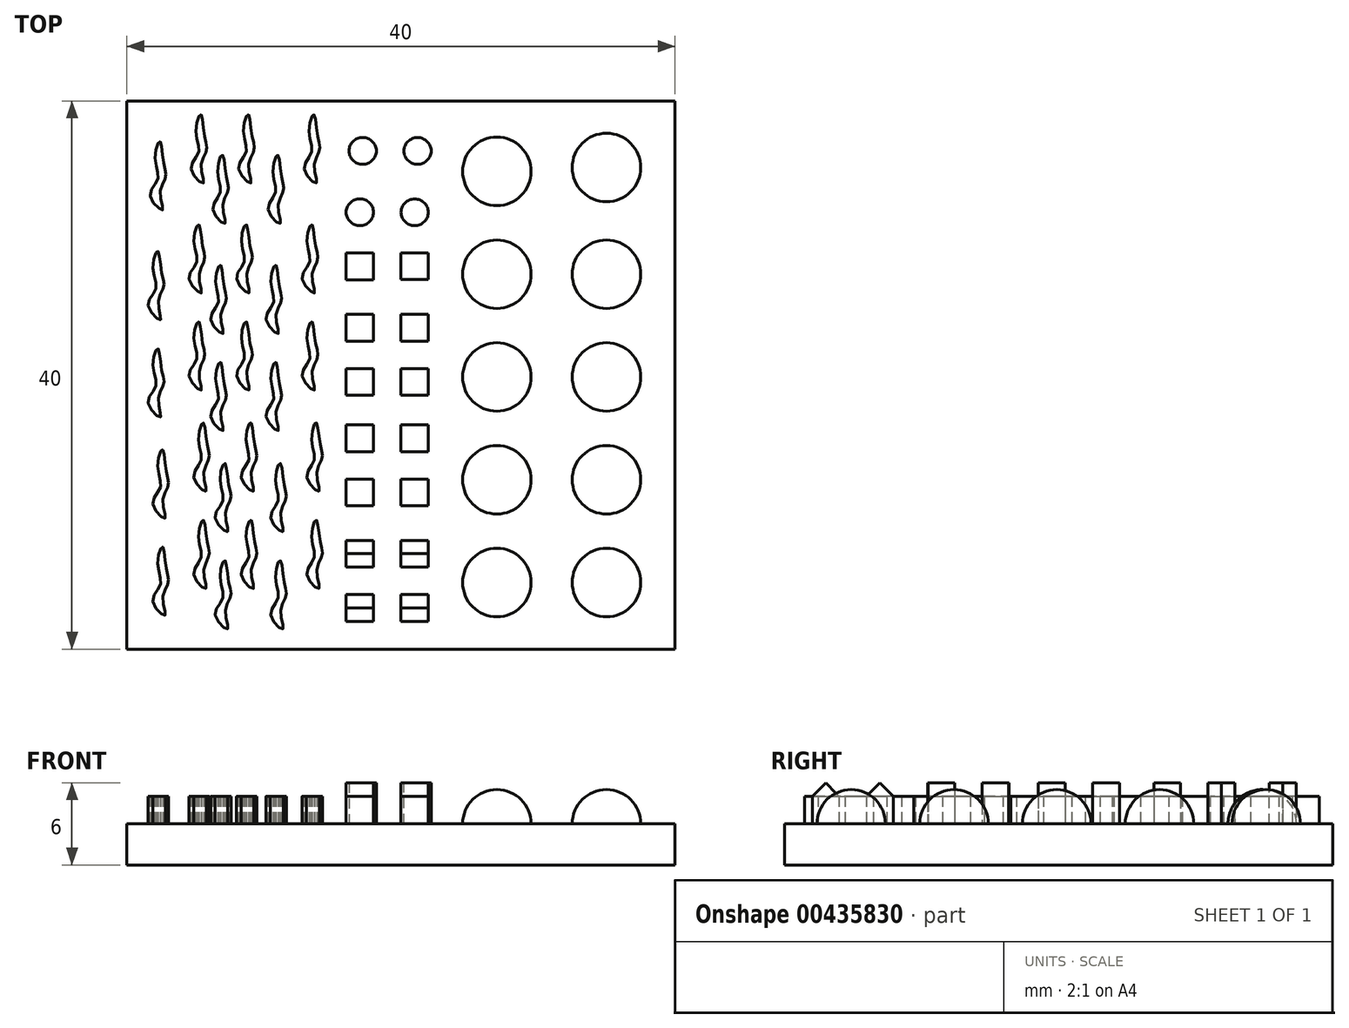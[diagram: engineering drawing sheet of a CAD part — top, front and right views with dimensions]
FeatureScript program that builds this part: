
annotation { "Feature Type Name" : "Feature", "Feature Type Description" : "" }
export const myFeature = defineFeature(function(context is Context, id is Id, definition is map)
    precondition{}
    {
        {
            var Q0;
            Q0=qCreatedBy(makeId("Top.planeOp"),FACE);
            var sketch = newSketch(context, id + "F0", { "sketchPlane" : qUnion([Q0])});
            skLineSegment(sketch, "E0.bottom", {"start": v(0, 0) * mm, "end": v(-40, 0) * mm});
            skLineSegment(sketch, "E0.top", {"start": v(0, 40) * mm, "end": v(-40, 40) * mm});
            skLineSegment(sketch, "E0.left", {"start": v(0, 0) * mm, "end": v(0, 40) * mm});
            skLineSegment(sketch, "E0.right", {"start": v(-40, 0) * mm, "end": v(-40, 40) * mm});
            skSolve(sketch);
        }
        {
            var Q0;
            Q0 = qSketchRegion(id + "F0", true);
            extrude(context, id + "F1", {"entities" : qUnion([Q0]), "depth" : 3 * mm});
        }
        {
            var Q0;
            Q0=makeQuery(id+"F1.opExtrude","CAP_FACE",FACE,{"disambiguationData":[OSD([sQuery(id+"F0.wireOp",EDGE,"E0.bottom"),sQuery(id+"F0.wireOp",EDGE,"E0.top"),sQuery(id+"F0.wireOp",EDGE,"E0.left"),sQuery(id+"F0.wireOp",EDGE,"E0.right")])],"isStart":false});
            var sketch = newSketch(context, id + "F2", { "sketchPlane" : qUnion([Q0])});
            skLineSegment(sketch, "E1", {"start": v(0, 0) * mm, "end": v(-10, 0) * mm});
            skPoint(sketch, "E2.end.orphan", {"position": v(-5, 0) * mm});
            skLineSegment(sketch, "E3", {"start": v(0, 0) * mm, "end": v(-5, 0) * mm});
            skArc(sketch, "E4", {"start": v(-5, 32.64) * mm, "mid": v(-2.5, 35.14) * mm, "end": v(-5, 37.64) * mm});
            skLineSegment(sketch, "E5", {"start": v(-5, 37.64) * mm, "end": v(-5, 40) * mm});
            skLineSegment(sketch, "E6", {"start": v(-5, 37.64) * mm, "end": v(-5, 32.64) * mm, "construction": true});
            skLineSegment(sketch, "E7", {"start": v(-5, 37.64) * mm, "end": v(-5, 32.64) * mm});
            skLineSegment(sketch, "E8", {"start": v(-5, 32.64) * mm, "end": v(-5, 30.14) * mm});
            skLineSegment(sketch, "E9", {"start": v(-5, 40) * mm, "end": v(0, 40) * mm});
            skSolve(sketch);
        }
        {
            var Q0;
            Q0=makeQuery(id+"F1.opExtrude","CAP_FACE",FACE,{"disambiguationData":[OSD([sQuery(id+"F0.wireOp",EDGE,"E0.bottom"),sQuery(id+"F0.wireOp",EDGE,"E0.top"),sQuery(id+"F0.wireOp",EDGE,"E0.left"),sQuery(id+"F0.wireOp",EDGE,"E0.right")])],"isStart":false});
            var sketch = newSketch(context, id + "F3", { "sketchPlane" : qUnion([Q0])});
            skFitSpline(sketch, "E10", {"points": [v(-37.76, 6.25) * mm, v(-37.56, 4.7) * mm, v(-38.1, 3.49) * mm, v(-37.23, 2.46) * mm, v(-37.38, 3.69) * mm, v(-36.98, 4.9) * mm, v(-37.13, 5.9) * mm, v(-37.41, 7.46) * mm, v(-37.76, 6.25) * mm]});
            skFitSpline(sketch, "E11", {"points": [v(-37.76, 13.34) * mm, v(-37.56, 11.8) * mm, v(-38.1, 10.58) * mm, v(-37.23, 9.55) * mm, v(-37.38, 10.78) * mm, v(-36.98, 11.98) * mm, v(-37.13, 13) * mm, v(-37.41, 14.56) * mm, v(-37.76, 13.34) * mm]});
            skFitSpline(sketch, "E12", {"points": [v(-38.1, 20.72) * mm, v(-37.9, 19.17) * mm, v(-38.44, 17.96) * mm, v(-37.56, 16.93) * mm, v(-37.72, 18.16) * mm, v(-37.31, 19.36) * mm, v(-37.46, 20.38) * mm, v(-37.75, 21.94) * mm, v(-38.1, 20.72) * mm]});
            skFitSpline(sketch, "E13", {"points": [v(-38.1, 27.81) * mm, v(-37.9, 26.26) * mm, v(-38.44, 25.05) * mm, v(-37.56, 24.02) * mm, v(-37.72, 25.25) * mm, v(-37.31, 26.45) * mm, v(-37.46, 27.47) * mm, v(-37.75, 29.03) * mm, v(-38.1, 27.81) * mm]});
            skFitSpline(sketch, "E14", {"points": [v(-37.94, 35.84) * mm, v(-37.75, 34.29) * mm, v(-38.3, 33.07) * mm, v(-37.41, 32.05) * mm, v(-37.57, 33.27) * mm, v(-37.16, 34.48) * mm, v(-37.32, 35.5) * mm, v(-37.6, 37.05) * mm, v(-37.94, 35.84) * mm]});
            skFitSpline(sketch, "E15", {"points": [v(-34.78, 8.21) * mm, v(-34.58, 6.66) * mm, v(-35.13, 5.45) * mm, v(-34.25, 4.42) * mm, v(-34.4, 5.65) * mm, v(-34, 6.85) * mm, v(-34.15, 7.87) * mm, v(-34.44, 9.42) * mm, v(-34.78, 8.21) * mm]});
            skFitSpline(sketch, "E16", {"points": [v(-34.78, 15.3) * mm, v(-34.58, 13.75) * mm, v(-35.13, 12.54) * mm, v(-34.25, 11.5) * mm, v(-34.4, 12.74) * mm, v(-34, 13.94) * mm, v(-34.15, 14.96) * mm, v(-34.44, 16.52) * mm, v(-34.78, 15.3) * mm]});
            skFitSpline(sketch, "E17", {"points": [v(-35.11, 22.68) * mm, v(-34.92, 21.13) * mm, v(-35.46, 19.92) * mm, v(-34.58, 18.9) * mm, v(-34.74, 20.12) * mm, v(-34.33, 21.32) * mm, v(-34.48, 22.34) * mm, v(-34.77, 23.9) * mm, v(-35.11, 22.68) * mm]});
            skFitSpline(sketch, "E18", {"points": [v(-35.11, 29.77) * mm, v(-34.92, 28.22) * mm, v(-35.46, 27.01) * mm, v(-34.58, 25.98) * mm, v(-34.74, 27.2) * mm, v(-34.33, 28.41) * mm, v(-34.48, 29.43) * mm, v(-34.77, 30.99) * mm, v(-35.11, 29.77) * mm]});
            skFitSpline(sketch, "E19", {"points": [v(-34.97, 37.8) * mm, v(-34.77, 36.25) * mm, v(-35.31, 35.03) * mm, v(-34.44, 34) * mm, v(-34.59, 35.23) * mm, v(-34.18, 36.44) * mm, v(-34.34, 37.45) * mm, v(-34.62, 39.01) * mm, v(-34.97, 37.8) * mm]});
            skFitSpline(sketch, "E20", {"points": [v(-33.2, 5.26) * mm, v(-33, 3.7) * mm, v(-33.55, 2.5) * mm, v(-32.67, 1.46) * mm, v(-32.82, 2.69) * mm, v(-32.42, 3.9) * mm, v(-32.57, 4.91) * mm, v(-32.86, 6.47) * mm, v(-33.2, 5.26) * mm]});
            skFitSpline(sketch, "E21", {"points": [v(-33.2, 12.35) * mm, v(-33, 10.8) * mm, v(-33.55, 9.58) * mm, v(-32.67, 8.55) * mm, v(-32.82, 9.78) * mm, v(-32.42, 10.99) * mm, v(-32.57, 12) * mm, v(-32.86, 13.56) * mm, v(-33.2, 12.35) * mm]});
            skFitSpline(sketch, "E22", {"points": [v(-33.53, 19.73) * mm, v(-33.34, 18.18) * mm, v(-33.88, 16.97) * mm, v(-33, 15.94) * mm, v(-33.16, 17.16) * mm, v(-32.75, 18.37) * mm, v(-32.9, 19.38) * mm, v(-33.19, 20.94) * mm, v(-33.53, 19.73) * mm]});
            skFitSpline(sketch, "E23", {"points": [v(-33.53, 26.82) * mm, v(-33.34, 25.27) * mm, v(-33.88, 24.06) * mm, v(-33, 23.03) * mm, v(-33.16, 24.25) * mm, v(-32.75, 25.46) * mm, v(-32.9, 26.47) * mm, v(-33.19, 28.03) * mm, v(-33.53, 26.82) * mm]});
            skFitSpline(sketch, "E24", {"points": [v(-33.39, 34.84) * mm, v(-33.19, 33.3) * mm, v(-33.73, 32.08) * mm, v(-32.86, 31.05) * mm, v(-33, 32.28) * mm, v(-32.6, 33.48) * mm, v(-32.76, 34.5) * mm, v(-33.04, 36.06) * mm, v(-33.39, 34.84) * mm]});
            skFitSpline(sketch, "E25", {"points": [v(-31.3, 8.21) * mm, v(-31.11, 6.66) * mm, v(-31.66, 5.45) * mm, v(-30.78, 4.42) * mm, v(-30.93, 5.65) * mm, v(-30.53, 6.85) * mm, v(-30.68, 7.87) * mm, v(-30.97, 9.42) * mm, v(-31.3, 8.21) * mm]});
            skFitSpline(sketch, "E26", {"points": [v(-31.3, 15.3) * mm, v(-31.11, 13.75) * mm, v(-31.66, 12.54) * mm, v(-30.78, 11.5) * mm, v(-30.93, 12.74) * mm, v(-30.53, 13.94) * mm, v(-30.68, 14.96) * mm, v(-30.97, 16.52) * mm, v(-31.3, 15.3) * mm]});
            skFitSpline(sketch, "E27", {"points": [v(-31.64, 22.68) * mm, v(-31.45, 21.13) * mm, v(-32, 19.92) * mm, v(-31.11, 18.9) * mm, v(-31.27, 20.12) * mm, v(-30.86, 21.32) * mm, v(-31.02, 22.34) * mm, v(-31.3, 23.9) * mm, v(-31.64, 22.68) * mm]});
            skFitSpline(sketch, "E28", {"points": [v(-31.64, 29.77) * mm, v(-31.45, 28.22) * mm, v(-32, 27.01) * mm, v(-31.11, 25.98) * mm, v(-31.27, 27.2) * mm, v(-30.86, 28.41) * mm, v(-31.02, 29.43) * mm, v(-31.3, 30.99) * mm, v(-31.64, 29.77) * mm]});
            skFitSpline(sketch, "E29", {"points": [v(-31.5, 37.8) * mm, v(-31.3, 36.25) * mm, v(-31.85, 35.03) * mm, v(-30.97, 34) * mm, v(-31.12, 35.23) * mm, v(-30.71, 36.44) * mm, v(-30.87, 37.45) * mm, v(-31.15, 39.01) * mm, v(-31.5, 37.8) * mm]});
            skFitSpline(sketch, "E30", {"points": [v(-29.16, 5.26) * mm, v(-28.97, 3.7) * mm, v(-29.51, 2.5) * mm, v(-28.63, 1.46) * mm, v(-28.79, 2.69) * mm, v(-28.38, 3.9) * mm, v(-28.54, 4.91) * mm, v(-28.82, 6.47) * mm, v(-29.16, 5.26) * mm]});
            skFitSpline(sketch, "E31", {"points": [v(-29.16, 12.35) * mm, v(-28.97, 10.8) * mm, v(-29.51, 9.58) * mm, v(-28.63, 8.55) * mm, v(-28.79, 9.78) * mm, v(-28.38, 10.99) * mm, v(-28.54, 12) * mm, v(-28.82, 13.56) * mm, v(-29.16, 12.35) * mm]});
            skFitSpline(sketch, "E32", {"points": [v(-29.5, 19.73) * mm, v(-29.3, 18.18) * mm, v(-29.85, 16.97) * mm, v(-28.97, 15.94) * mm, v(-29.12, 17.16) * mm, v(-28.72, 18.37) * mm, v(-28.87, 19.38) * mm, v(-29.15, 20.94) * mm, v(-29.5, 19.73) * mm]});
            skFitSpline(sketch, "E33", {"points": [v(-29.5, 26.82) * mm, v(-29.3, 25.27) * mm, v(-29.85, 24.06) * mm, v(-28.97, 23.03) * mm, v(-29.12, 24.25) * mm, v(-28.72, 25.46) * mm, v(-28.87, 26.47) * mm, v(-29.15, 28.03) * mm, v(-29.5, 26.82) * mm]});
            skFitSpline(sketch, "E34", {"points": [v(-29.35, 34.84) * mm, v(-29.15, 33.3) * mm, v(-29.7, 32.08) * mm, v(-28.82, 31.05) * mm, v(-28.97, 32.28) * mm, v(-28.57, 33.48) * mm, v(-28.72, 34.5) * mm, v(-29, 36.06) * mm, v(-29.35, 34.84) * mm]});
            skFitSpline(sketch, "E35", {"points": [v(-26.53, 8.21) * mm, v(-26.33, 6.66) * mm, v(-26.88, 5.45) * mm, v(-26, 4.42) * mm, v(-26.15, 5.65) * mm, v(-25.75, 6.85) * mm, v(-25.9, 7.87) * mm, v(-26.18, 9.42) * mm, v(-26.53, 8.21) * mm]});
            skFitSpline(sketch, "E36", {"points": [v(-26.53, 15.3) * mm, v(-26.33, 13.75) * mm, v(-26.88, 12.54) * mm, v(-26, 11.5) * mm, v(-26.15, 12.74) * mm, v(-25.75, 13.94) * mm, v(-25.9, 14.96) * mm, v(-26.18, 16.52) * mm, v(-26.53, 15.3) * mm]});
            skFitSpline(sketch, "E37", {"points": [v(-26.86, 22.68) * mm, v(-26.67, 21.13) * mm, v(-27.21, 19.92) * mm, v(-26.33, 18.9) * mm, v(-26.49, 20.12) * mm, v(-26.08, 21.32) * mm, v(-26.23, 22.34) * mm, v(-26.52, 23.9) * mm, v(-26.86, 22.68) * mm]});
            skFitSpline(sketch, "E38", {"points": [v(-26.86, 29.77) * mm, v(-26.67, 28.22) * mm, v(-27.21, 27.01) * mm, v(-26.33, 25.98) * mm, v(-26.49, 27.2) * mm, v(-26.08, 28.41) * mm, v(-26.23, 29.43) * mm, v(-26.52, 30.99) * mm, v(-26.86, 29.77) * mm]});
            skFitSpline(sketch, "E39", {"points": [v(-26.71, 37.8) * mm, v(-26.52, 36.25) * mm, v(-27.06, 35.03) * mm, v(-26.18, 34) * mm, v(-26.34, 35.23) * mm, v(-25.93, 36.44) * mm, v(-26.09, 37.45) * mm, v(-26.37, 39.01) * mm, v(-26.71, 37.8) * mm]});
            skSolve(sketch);
        }
        {
            var Q0;
            Q0 = qSketchRegion(id + "F3", true);
            extrude(context, id + "F4", {"entities" : qUnion([Q0]), "operationType" : NewBodyOperationType.ADD, "depth" : 2 * mm});
        }
        {
            var Q0;
            Q0=makeQuery(id+"F2.imprint","IMPRINT",FACE,{"disambiguationData":[TD([[makeQuery(id+"F2.imprint","IMPRINT",EDGE,{"derivedFrom":sQuery(id+"F2.wireOp",EDGE,"E4")}),1.0]])]});
            var Q1;
            Q1=sQuery(id+"F2.wireOp",EDGE,"E7");
            revolve(context, id + "F5", {"operationType" : NewBodyOperationType.ADD, "entities" : qUnion([Q0]), "axis" : qUnion([Q1]), "revolveType" : RevolveType.FULL});
        }
        {
            var Q0;
            Q0=makeQuery(id+"F1.opExtrude","CAP_FACE",FACE,{"disambiguationData":[OSD([sQuery(id+"F0.wireOp",EDGE,"E0.bottom"),sQuery(id+"F0.wireOp",EDGE,"E0.top"),sQuery(id+"F0.wireOp",EDGE,"E0.left"),sQuery(id+"F0.wireOp",EDGE,"E0.right")])],"isStart":false});
            var sketch = newSketch(context, id + "F6", { "sketchPlane" : qUnion([Q0])});
            skLineSegment(sketch, "E40", {"start": v(0, 0) * mm, "end": v(-5, 0) * mm});
            skLineSegment(sketch, "E41", {"start": v(-5, 0) * mm, "end": v(-5, 2.36) * mm});
            skArc(sketch, "E42", {"start": v(-5, 2.36) * mm, "mid": v(-2.5, 4.86) * mm, "end": v(-5, 7.36) * mm});
            skLineSegment(sketch, "E43", {"start": v(-5, 2.36) * mm, "end": v(-5, 7.36) * mm});
            skLineSegment(sketch, "E44", {"start": v(-5, 7.36) * mm, "end": v(-5, 2.36) * mm, "construction": true});
            skSolve(sketch);
        }
        {
            var Q0;
            Q0 = qSketchRegion(id + "F6", true);
            var Q1;
            Q1=sQuery(id+"F6.wireOp",EDGE,"E43");
            revolve(context, id + "F7", {"operationType" : NewBodyOperationType.ADD, "entities" : qUnion([Q0]), "axis" : qUnion([Q1]), "revolveType" : RevolveType.FULL});
        }
        {
            var Q0;
            Q0=makeQuery(id+"F1.opExtrude","CAP_FACE",FACE,{"disambiguationData":[OSD([sQuery(id+"F0.wireOp",EDGE,"E0.bottom"),sQuery(id+"F0.wireOp",EDGE,"E0.top"),sQuery(id+"F0.wireOp",EDGE,"E0.left"),sQuery(id+"F0.wireOp",EDGE,"E0.right")])],"isStart":false});
            var sketch = newSketch(context, id + "F8", { "sketchPlane" : qUnion([Q0])});
            skLineSegment(sketch, "E45", {"start": v(0, 0) * mm, "end": v(-5, 0) * mm});
            skLineSegment(sketch, "E46", {"start": v(-5, 0) * mm, "end": v(-5, 7.36) * mm});
            skLineSegment(sketch, "E47", {"start": v(-5, 7.36) * mm, "end": v(-5, 9.86) * mm});
            skArc(sketch, "E48", {"start": v(-5, 9.86) * mm, "mid": v(-2.5, 12.36) * mm, "end": v(-5, 14.86) * mm});
            skLineSegment(sketch, "E49", {"start": v(-5, 9.86) * mm, "end": v(-5, 14.86) * mm});
            skLineSegment(sketch, "E50", {"start": v(-5, 14.86) * mm, "end": v(-5, 9.86) * mm, "construction": true});
            skSolve(sketch);
        }
        {
            var Q0;
            Q0 = qSketchRegion(id + "F8", true);
            var Q1;
            Q1=sQuery(id+"F8.wireOp",EDGE,"E49");
            revolve(context, id + "F9", {"operationType" : NewBodyOperationType.ADD, "entities" : qUnion([Q0]), "axis" : qUnion([Q1]), "revolveType" : RevolveType.FULL});
        }
        {
            var Q0;
            Q0=makeQuery(id+"F1.opExtrude","CAP_FACE",FACE,{"disambiguationData":[OSD([sQuery(id+"F0.wireOp",EDGE,"E0.bottom"),sQuery(id+"F0.wireOp",EDGE,"E0.top"),sQuery(id+"F0.wireOp",EDGE,"E0.left"),sQuery(id+"F0.wireOp",EDGE,"E0.right")])],"isStart":false});
            var sketch = newSketch(context, id + "F10", { "sketchPlane" : qUnion([Q0])});
            skLineSegment(sketch, "E51", {"start": v(0, 0) * mm, "end": v(-5, 0) * mm});
            skLineSegment(sketch, "E52", {"start": v(-5, 0) * mm, "end": v(-5, 14.86) * mm});
            skLineSegment(sketch, "E53", {"start": v(-5, 14.86) * mm, "end": v(-5, 17.36) * mm});
            skArc(sketch, "E54", {"start": v(-5, 17.36) * mm, "mid": v(-2.5, 19.86) * mm, "end": v(-5, 22.36) * mm});
            skLineSegment(sketch, "E55", {"start": v(-5, 17.36) * mm, "end": v(-5, 22.36) * mm});
            skLineSegment(sketch, "E56", {"start": v(-5, 22.36) * mm, "end": v(-5, 17.36) * mm, "construction": true});
            skSolve(sketch);
        }
        {
            var Q0;
            Q0 = qSketchRegion(id + "F10", true);
            var Q1;
            Q1=sQuery(id+"F10.wireOp",EDGE,"E55");
            revolve(context, id + "F11", {"operationType" : NewBodyOperationType.ADD, "entities" : qUnion([Q0]), "axis" : qUnion([Q1]), "revolveType" : RevolveType.FULL});
        }
        {
            var Q0;
            Q0=makeQuery(id+"F1.opExtrude","CAP_FACE",FACE,{"disambiguationData":[OSD([sQuery(id+"F0.wireOp",EDGE,"E0.bottom"),sQuery(id+"F0.wireOp",EDGE,"E0.top"),sQuery(id+"F0.wireOp",EDGE,"E0.left"),sQuery(id+"F0.wireOp",EDGE,"E0.right")])],"isStart":false});
            var sketch = newSketch(context, id + "F12", { "sketchPlane" : qUnion([Q0])});
            skLineSegment(sketch, "E57", {"start": v(0, 0) * mm, "end": v(-5, 0) * mm});
            skLineSegment(sketch, "E58", {"start": v(-5, 0) * mm, "end": v(-5, 22.36) * mm});
            skLineSegment(sketch, "E59", {"start": v(-5, 22.36) * mm, "end": v(-5, 24.86) * mm});
            skArc(sketch, "E60", {"start": v(-5, 24.86) * mm, "mid": v(-2.5, 27.36) * mm, "end": v(-5, 29.86) * mm});
            skLineSegment(sketch, "E61", {"start": v(-5, 24.86) * mm, "end": v(-5, 29.86) * mm});
            skLineSegment(sketch, "E62", {"start": v(-5, 29.86) * mm, "end": v(-5, 24.86) * mm, "construction": true});
            skSolve(sketch);
        }
        {
            var Q0;
            Q0 = qSketchRegion(id + "F12", true);
            var Q1;
            Q1=sQuery(id+"F12.wireOp",EDGE,"E61");
            revolve(context, id + "F13", {"operationType" : NewBodyOperationType.ADD, "entities" : qUnion([Q0]), "axis" : qUnion([Q1]), "revolveType" : RevolveType.FULL});
        }
        {
            var Q0;
            Q0=makeQuery(id+"F1.opExtrude","CAP_FACE",FACE,{"disambiguationData":[OSD([sQuery(id+"F0.wireOp",EDGE,"E0.bottom"),sQuery(id+"F0.wireOp",EDGE,"E0.top"),sQuery(id+"F0.wireOp",EDGE,"E0.left"),sQuery(id+"F0.wireOp",EDGE,"E0.right")])],"isStart":false});
            var sketch = newSketch(context, id + "F14", { "sketchPlane" : qUnion([Q0])});
            skLineSegment(sketch, "E63", {"start": v(0, 0) * mm, "end": v(-13, 0) * mm});
            skLineSegment(sketch, "E64", {"start": v(-13, 0) * mm, "end": v(-13, 2.36) * mm});
            skArc(sketch, "E65", {"start": v(-13, 2.36) * mm, "mid": v(-10.5, 4.86) * mm, "end": v(-13, 7.36) * mm});
            skLineSegment(sketch, "E66", {"start": v(-13, 2.36) * mm, "end": v(-13, 7.36) * mm});
            skLineSegment(sketch, "E67", {"start": v(-13, 7.36) * mm, "end": v(-13, 2.36) * mm, "construction": true});
            skSolve(sketch);
        }
        {
            var Q0;
            Q0 = qSketchRegion(id + "F14", true);
            var Q1;
            Q1=sQuery(id+"F14.wireOp",EDGE,"E66");
            revolve(context, id + "F15", {"operationType" : NewBodyOperationType.ADD, "entities" : qUnion([Q0]), "axis" : qUnion([Q1]), "revolveType" : RevolveType.FULL});
        }
        {
            var Q0;
            Q0=makeQuery(id+"F1.opExtrude","CAP_FACE",FACE,{"disambiguationData":[OSD([sQuery(id+"F0.wireOp",EDGE,"E0.bottom"),sQuery(id+"F0.wireOp",EDGE,"E0.top"),sQuery(id+"F0.wireOp",EDGE,"E0.left"),sQuery(id+"F0.wireOp",EDGE,"E0.right")])],"isStart":false});
            var sketch = newSketch(context, id + "F16", { "sketchPlane" : qUnion([Q0])});
            skLineSegment(sketch, "E68", {"start": v(0, 0) * mm, "end": v(-13, 0) * mm});
            skLineSegment(sketch, "E69", {"start": v(-13, 0) * mm, "end": v(-13, 7.36) * mm});
            skLineSegment(sketch, "E70", {"start": v(-13, 7.36) * mm, "end": v(-13, 9.86) * mm});
            skArc(sketch, "E71", {"start": v(-13, 9.86) * mm, "mid": v(-10.5, 12.36) * mm, "end": v(-13, 14.86) * mm});
            skLineSegment(sketch, "E72", {"start": v(-13, 9.86) * mm, "end": v(-13, 14.86) * mm});
            skLineSegment(sketch, "E73", {"start": v(-13, 14.86) * mm, "end": v(-13, 9.86) * mm, "construction": true});
            skSolve(sketch);
        }
        {
            var Q0;
            Q0 = qSketchRegion(id + "F16", true);
            var Q1;
            Q1=sQuery(id+"F16.wireOp",EDGE,"E72");
            revolve(context, id + "F17", {"operationType" : NewBodyOperationType.ADD, "entities" : qUnion([Q0]), "axis" : qUnion([Q1]), "revolveType" : RevolveType.FULL});
        }
        {
            var Q0;
            Q0=makeQuery(id+"F1.opExtrude","CAP_FACE",FACE,{"disambiguationData":[OSD([sQuery(id+"F0.wireOp",EDGE,"E0.bottom"),sQuery(id+"F0.wireOp",EDGE,"E0.top"),sQuery(id+"F0.wireOp",EDGE,"E0.left"),sQuery(id+"F0.wireOp",EDGE,"E0.right")])],"isStart":false});
            var sketch = newSketch(context, id + "F18", { "sketchPlane" : qUnion([Q0])});
            skLineSegment(sketch, "E74", {"start": v(0, 0) * mm, "end": v(-13, 0) * mm});
            skLineSegment(sketch, "E75", {"start": v(-13, 0) * mm, "end": v(-13, 14.86) * mm});
            skLineSegment(sketch, "E76", {"start": v(-13, 14.86) * mm, "end": v(-13, 17.36) * mm});
            skArc(sketch, "E77", {"start": v(-13, 17.36) * mm, "mid": v(-10.5, 19.86) * mm, "end": v(-13, 22.36) * mm});
            skLineSegment(sketch, "E78", {"start": v(-13, 17.36) * mm, "end": v(-13, 22.36) * mm});
            skLineSegment(sketch, "E79", {"start": v(-13, 22.36) * mm, "end": v(-13, 17.36) * mm, "construction": true});
            skSolve(sketch);
        }
        {
            var Q0;
            Q0 = qSketchRegion(id + "F18", true);
            var Q1;
            Q1=sQuery(id+"F18.wireOp",EDGE,"E78");
            revolve(context, id + "F19", {"operationType" : NewBodyOperationType.ADD, "entities" : qUnion([Q0]), "axis" : qUnion([Q1]), "revolveType" : RevolveType.FULL});
        }
        {
            var Q0;
            Q0=makeQuery(id+"F1.opExtrude","CAP_FACE",FACE,{"disambiguationData":[OSD([sQuery(id+"F0.wireOp",EDGE,"E0.bottom"),sQuery(id+"F0.wireOp",EDGE,"E0.top"),sQuery(id+"F0.wireOp",EDGE,"E0.left"),sQuery(id+"F0.wireOp",EDGE,"E0.right")])],"isStart":false});
            var sketch = newSketch(context, id + "F20", { "sketchPlane" : qUnion([Q0])});
            skLineSegment(sketch, "E80", {"start": v(0, 0) * mm, "end": v(-13, 0) * mm});
            skLineSegment(sketch, "E81", {"start": v(-13, 0) * mm, "end": v(-13, 22.36) * mm});
            skLineSegment(sketch, "E82", {"start": v(-13, 22.36) * mm, "end": v(-13, 24.86) * mm});
            skArc(sketch, "E83", {"start": v(-13, 24.86) * mm, "mid": v(-10.5, 27.36) * mm, "end": v(-13, 29.86) * mm});
            skLineSegment(sketch, "E84", {"start": v(-13, 24.86) * mm, "end": v(-13, 29.86) * mm});
            skLineSegment(sketch, "E85", {"start": v(-13, 29.86) * mm, "end": v(-13, 24.86) * mm, "construction": true});
            skSolve(sketch);
        }
        {
            var Q0;
            Q0 = qSketchRegion(id + "F20", true);
            var Q1;
            Q1=sQuery(id+"F20.wireOp",EDGE,"E84");
            revolve(context, id + "F21", {"operationType" : NewBodyOperationType.ADD, "entities" : qUnion([Q0]), "axis" : qUnion([Q1]), "revolveType" : RevolveType.FULL});
        }
        {
            var Q0;
            Q0=makeQuery(id+"F1.opExtrude","CAP_FACE",FACE,{"disambiguationData":[OSD([sQuery(id+"F0.wireOp",EDGE,"E0.bottom"),sQuery(id+"F0.wireOp",EDGE,"E0.top"),sQuery(id+"F0.wireOp",EDGE,"E0.left"),sQuery(id+"F0.wireOp",EDGE,"E0.right")])],"isStart":false});
            var sketch = newSketch(context, id + "F22", { "sketchPlane" : qUnion([Q0])});
            skLineSegment(sketch, "E86", {"start": v(0, 0) * mm, "end": v(-13, 0) * mm});
            skLineSegment(sketch, "E87", {"start": v(-13, 0) * mm, "end": v(-13, 29.86) * mm});
            skArc(sketch, "E88", {"start": v(-13, 32.36) * mm, "mid": v(-10.5, 34.86) * mm, "end": v(-13, 37.36) * mm});
            skLineSegment(sketch, "E89", {"start": v(-13, 32.36) * mm, "end": v(-13, 37.36) * mm});
            skLineSegment(sketch, "E90", {"start": v(-13, 37.36) * mm, "end": v(-13, 32.36) * mm, "construction": true});
            skSolve(sketch);
        }
        {
            var Q0;
            Q0 = qSketchRegion(id + "F22", true);
            var Q1;
            Q1=sQuery(id+"F22.wireOp",EDGE,"E89");
            revolve(context, id + "F23", {"operationType" : NewBodyOperationType.ADD, "entities" : qUnion([Q0]), "axis" : qUnion([Q1]), "revolveType" : RevolveType.FULL});
        }
        {
            var Q0;
            Q0=makeQuery(id+"F1.opExtrude","CAP_FACE",FACE,{"disambiguationData":[OSD([sQuery(id+"F0.wireOp",EDGE,"E0.bottom"),sQuery(id+"F0.wireOp",EDGE,"E0.top"),sQuery(id+"F0.wireOp",EDGE,"E0.left"),sQuery(id+"F0.wireOp",EDGE,"E0.right")])],"isStart":false});
            var sketch = newSketch(context, id + "F24", { "sketchPlane" : qUnion([Q0])});
            skLineSegment(sketch, "E91", {"start": v(0, 0) * mm, "end": v(-21, 0) * mm});
            skLineSegment(sketch, "E92", {"start": v(-21, 0) * mm, "end": v(-21, 3) * mm});
            skLineSegment(sketch, "E93.bottom", {"start": v(-22, 2.02) * mm, "end": v(-24, 2.02) * mm});
            skLineSegment(sketch, "E93.top", {"start": v(-22, 3.98) * mm, "end": v(-24, 3.98) * mm});
            skLineSegment(sketch, "E93.left", {"start": v(-22, 2.02) * mm, "end": v(-22, 3.98) * mm});
            skLineSegment(sketch, "E93.right", {"start": v(-24, 2.02) * mm, "end": v(-24, 3.98) * mm});
            skPoint(sketch, "E93.middle", {"position": v(-23, 3) * mm});
            skLineSegment(sketch, "E94.bottom", {"start": v(-18, 2.02) * mm, "end": v(-20, 2.02) * mm});
            skLineSegment(sketch, "E94.top", {"start": v(-18, 3.98) * mm, "end": v(-20, 3.98) * mm});
            skLineSegment(sketch, "E94.left", {"start": v(-18, 2.02) * mm, "end": v(-18, 3.98) * mm});
            skLineSegment(sketch, "E94.right", {"start": v(-20, 2.02) * mm, "end": v(-20, 3.98) * mm});
            skPoint(sketch, "E94.middle", {"position": v(-19, 3) * mm});
            skLineSegment(sketch, "E95.bottom", {"start": v(-22, 5.98) * mm, "end": v(-24, 5.98) * mm});
            skLineSegment(sketch, "E95.top", {"start": v(-22, 7.94) * mm, "end": v(-24, 7.94) * mm});
            skLineSegment(sketch, "E95.left", {"start": v(-22, 5.98) * mm, "end": v(-22, 7.94) * mm});
            skLineSegment(sketch, "E95.right", {"start": v(-24, 5.98) * mm, "end": v(-24, 7.94) * mm});
            skLineSegment(sketch, "E96.bottom", {"start": v(-18, 5.98) * mm, "end": v(-20, 5.98) * mm});
            skLineSegment(sketch, "E96.top", {"start": v(-18, 7.94) * mm, "end": v(-20, 7.94) * mm});
            skLineSegment(sketch, "E96.left", {"start": v(-18, 5.98) * mm, "end": v(-18, 7.94) * mm});
            skLineSegment(sketch, "E96.right", {"start": v(-20, 5.98) * mm, "end": v(-20, 7.94) * mm});
            skLineSegment(sketch, "E97.bottom", {"start": v(-22, 10.45) * mm, "end": v(-24, 10.45) * mm});
            skLineSegment(sketch, "E97.top", {"start": v(-22, 12.4) * mm, "end": v(-24, 12.4) * mm});
            skLineSegment(sketch, "E97.left", {"start": v(-22, 10.45) * mm, "end": v(-22, 12.4) * mm});
            skLineSegment(sketch, "E97.right", {"start": v(-24, 10.45) * mm, "end": v(-24, 12.4) * mm});
            skPoint(sketch, "E97.middle", {"position": v(-23, 11.43) * mm});
            skLineSegment(sketch, "E98.bottom", {"start": v(-18, 10.46) * mm, "end": v(-20, 10.46) * mm});
            skLineSegment(sketch, "E98.top", {"start": v(-18, 12.4) * mm, "end": v(-20, 12.4) * mm});
            skLineSegment(sketch, "E98.left", {"start": v(-18, 10.46) * mm, "end": v(-18, 12.4) * mm});
            skLineSegment(sketch, "E98.right", {"start": v(-20, 10.46) * mm, "end": v(-20, 12.4) * mm});
            skPoint(sketch, "E98.middle", {"position": v(-19, 11.43) * mm});
            skLineSegment(sketch, "E99.bottom", {"start": v(-22, 14.4) * mm, "end": v(-24, 14.4) * mm});
            skLineSegment(sketch, "E99.top", {"start": v(-22, 16.37) * mm, "end": v(-24, 16.37) * mm});
            skLineSegment(sketch, "E99.left", {"start": v(-22, 14.4) * mm, "end": v(-22, 16.37) * mm});
            skLineSegment(sketch, "E99.right", {"start": v(-24, 14.4) * mm, "end": v(-24, 16.37) * mm});
            skLineSegment(sketch, "E100.bottom", {"start": v(-18, 14.4) * mm, "end": v(-20, 14.4) * mm});
            skLineSegment(sketch, "E100.top", {"start": v(-18, 16.35) * mm, "end": v(-20, 16.35) * mm});
            skLineSegment(sketch, "E100.left", {"start": v(-18, 14.4) * mm, "end": v(-18, 16.35) * mm});
            skLineSegment(sketch, "E100.right", {"start": v(-20, 14.4) * mm, "end": v(-20, 16.35) * mm});
            skLineSegment(sketch, "E101.bottom", {"start": v(-22, 18.52) * mm, "end": v(-24, 18.52) * mm});
            skLineSegment(sketch, "E101.top", {"start": v(-22, 20.47) * mm, "end": v(-24, 20.47) * mm});
            skLineSegment(sketch, "E101.left", {"start": v(-22, 18.52) * mm, "end": v(-22, 20.47) * mm});
            skLineSegment(sketch, "E101.right", {"start": v(-24, 18.52) * mm, "end": v(-24, 20.47) * mm});
            skPoint(sketch, "E101.middle", {"position": v(-23, 19.5) * mm});
            skLineSegment(sketch, "E102.bottom", {"start": v(-18, 18.52) * mm, "end": v(-20, 18.52) * mm});
            skLineSegment(sketch, "E102.top", {"start": v(-18, 20.47) * mm, "end": v(-20, 20.47) * mm});
            skLineSegment(sketch, "E102.left", {"start": v(-18, 18.52) * mm, "end": v(-18, 20.47) * mm});
            skLineSegment(sketch, "E102.right", {"start": v(-20, 18.52) * mm, "end": v(-20, 20.47) * mm});
            skPoint(sketch, "E102.middle", {"position": v(-19, 19.5) * mm});
            skLineSegment(sketch, "E103", {"start": v(-21, 23.57) * mm, "end": v(-19, 23.57) * mm});
            skLineSegment(sketch, "E104.bottom", {"start": v(-22, 22.47) * mm, "end": v(-24, 22.47) * mm});
            skLineSegment(sketch, "E104.top", {"start": v(-22, 24.43) * mm, "end": v(-24, 24.43) * mm});
            skLineSegment(sketch, "E104.left", {"start": v(-22, 22.47) * mm, "end": v(-22, 24.43) * mm});
            skLineSegment(sketch, "E104.right", {"start": v(-24, 22.47) * mm, "end": v(-24, 24.43) * mm});
            skLineSegment(sketch, "E105.bottom", {"start": v(-18, 22.47) * mm, "end": v(-20, 22.47) * mm});
            skLineSegment(sketch, "E105.top", {"start": v(-18, 24.43) * mm, "end": v(-20, 24.43) * mm});
            skLineSegment(sketch, "E105.left", {"start": v(-18, 22.47) * mm, "end": v(-18, 24.43) * mm});
            skLineSegment(sketch, "E105.right", {"start": v(-20, 22.47) * mm, "end": v(-20, 24.43) * mm});
            skLineSegment(sketch, "E106.bottom", {"start": v(-22, 26.95) * mm, "end": v(-24, 26.95) * mm});
            skLineSegment(sketch, "E106.top", {"start": v(-22, 28.9) * mm, "end": v(-24, 28.9) * mm});
            skLineSegment(sketch, "E106.left", {"start": v(-22, 26.95) * mm, "end": v(-22, 28.9) * mm});
            skLineSegment(sketch, "E106.right", {"start": v(-24, 26.95) * mm, "end": v(-24, 28.9) * mm});
            skPoint(sketch, "E106.middle", {"position": v(-23, 27.92) * mm});
            skLineSegment(sketch, "E107.bottom", {"start": v(-18, 26.96) * mm, "end": v(-20, 26.96) * mm});
            skLineSegment(sketch, "E107.top", {"start": v(-18, 28.9) * mm, "end": v(-20, 28.9) * mm});
            skLineSegment(sketch, "E107.left", {"start": v(-18, 26.96) * mm, "end": v(-18, 28.9) * mm});
            skLineSegment(sketch, "E107.right", {"start": v(-20, 26.96) * mm, "end": v(-20, 28.9) * mm});
            skPoint(sketch, "E107.middle", {"position": v(-19, 27.93) * mm});
            skLineSegment(sketch, "E108.bottom", {"start": v(-22, 30.9) * mm, "end": v(-24, 30.9) * mm});
            skLineSegment(sketch, "E108.top", {"start": v(-22, 32.86) * mm, "end": v(-24, 32.86) * mm});
            skLineSegment(sketch, "E108.left", {"start": v(-22, 30.9) * mm, "end": v(-22, 32.86) * mm});
            skLineSegment(sketch, "E108.right", {"start": v(-24, 30.9) * mm, "end": v(-24, 32.86) * mm});
            skLineSegment(sketch, "E109.bottom", {"start": v(-18, 30.9) * mm, "end": v(-20, 30.9) * mm});
            skLineSegment(sketch, "E109.top", {"start": v(-18, 32.85) * mm, "end": v(-20, 32.85) * mm});
            skLineSegment(sketch, "E109.left", {"start": v(-18, 30.9) * mm, "end": v(-18, 32.85) * mm});
            skLineSegment(sketch, "E109.right", {"start": v(-20, 30.9) * mm, "end": v(-20, 32.85) * mm});
            skLineSegment(sketch, "E110.bottom", {"start": v(-21.8, 35.38) * mm, "end": v(-23.8, 35.38) * mm});
            skLineSegment(sketch, "E110.top", {"start": v(-21.8, 37.34) * mm, "end": v(-23.8, 37.34) * mm});
            skLineSegment(sketch, "E110.left", {"start": v(-21.8, 35.38) * mm, "end": v(-21.8, 37.34) * mm});
            skLineSegment(sketch, "E110.right", {"start": v(-23.8, 35.38) * mm, "end": v(-23.8, 37.34) * mm});
            skLineSegment(sketch, "E111.bottom", {"start": v(-17.8, 35.38) * mm, "end": v(-19.8, 35.38) * mm});
            skLineSegment(sketch, "E111.top", {"start": v(-17.8, 37.33) * mm, "end": v(-19.8, 37.33) * mm});
            skLineSegment(sketch, "E111.left", {"start": v(-17.8, 35.38) * mm, "end": v(-17.8, 37.33) * mm});
            skLineSegment(sketch, "E111.right", {"start": v(-19.8, 35.38) * mm, "end": v(-19.8, 37.33) * mm});
            skSolve(sketch);
        }
        {
            var Q0;
            Q0 = qSketchRegion(id + "F24", true);
            extrude(context, id + "F25", {"entities" : qUnion([Q0]), "operationType" : NewBodyOperationType.ADD, "depth" : 3 * mm});
        }
        {
            var Q0;
            Q0=makeQuery(id+"F25.opExtrude","SWEPT_EDGE",EDGE,{"disambiguationData":[OSD([sQuery(id+"F24.wireOp",EDGE,"E111.bottom"),sQuery(id+"F24.wireOp",EDGE,"E111.left")])]});
            var Q1;
            Q1=makeQuery(id+"F25.opExtrude","SWEPT_EDGE",EDGE,{"disambiguationData":[OSD([sQuery(id+"F24.wireOp",EDGE,"E111.top"),sQuery(id+"F24.wireOp",EDGE,"E111.right")])]});
            var Q2;
            Q2=makeQuery(id+"F25.opExtrude","SWEPT_EDGE",EDGE,{"disambiguationData":[OSD([sQuery(id+"F24.wireOp",EDGE,"E111.top"),sQuery(id+"F24.wireOp",EDGE,"E111.left")])]});
            var Q3;
            Q3=makeQuery(id+"F25.opExtrude","SWEPT_EDGE",EDGE,{"disambiguationData":[OSD([sQuery(id+"F24.wireOp",EDGE,"E111.bottom"),sQuery(id+"F24.wireOp",EDGE,"E111.right")])]});
            var Q4;
            Q4=makeQuery(id+"F25.opExtrude","SWEPT_EDGE",EDGE,{"disambiguationData":[OSD([sQuery(id+"F24.wireOp",EDGE,"E110.top"),sQuery(id+"F24.wireOp",EDGE,"E110.left")])]});
            var Q5;
            Q5=makeQuery(id+"F25.opExtrude","SWEPT_EDGE",EDGE,{"disambiguationData":[OSD([sQuery(id+"F24.wireOp",EDGE,"E110.bottom"),sQuery(id+"F24.wireOp",EDGE,"E110.left")])]});
            var Q6;
            Q6=makeQuery(id+"F25.opExtrude","SWEPT_EDGE",EDGE,{"disambiguationData":[OSD([sQuery(id+"F24.wireOp",EDGE,"E110.bottom"),sQuery(id+"F24.wireOp",EDGE,"E110.right")])]});
            var Q7;
            Q7=makeQuery(id+"F25.opExtrude","SWEPT_EDGE",EDGE,{"disambiguationData":[OSD([sQuery(id+"F24.wireOp",EDGE,"E110.top"),sQuery(id+"F24.wireOp",EDGE,"E110.right")])]});
            var Q8;
            Q8=makeQuery(id+"F25.opExtrude","SWEPT_EDGE",EDGE,{"disambiguationData":[OSD([sQuery(id+"F24.wireOp",EDGE,"E109.top"),sQuery(id+"F24.wireOp",EDGE,"E109.left")])]});
            var Q9;
            Q9=makeQuery(id+"F25.opExtrude","SWEPT_EDGE",EDGE,{"disambiguationData":[OSD([sQuery(id+"F24.wireOp",EDGE,"E109.bottom"),sQuery(id+"F24.wireOp",EDGE,"E109.left")])]});
            var Q10;
            Q10=makeQuery(id+"F25.opExtrude","SWEPT_EDGE",EDGE,{"disambiguationData":[OSD([sQuery(id+"F24.wireOp",EDGE,"E108.top"),sQuery(id+"F24.wireOp",EDGE,"E108.left")])]});
            var Q11;
            Q11=makeQuery(id+"F25.opExtrude","SWEPT_EDGE",EDGE,{"disambiguationData":[OSD([sQuery(id+"F24.wireOp",EDGE,"E109.bottom"),sQuery(id+"F24.wireOp",EDGE,"E109.right")])]});
            var Q12;
            Q12=makeQuery(id+"F25.opExtrude","SWEPT_EDGE",EDGE,{"disambiguationData":[OSD([sQuery(id+"F24.wireOp",EDGE,"E108.bottom"),sQuery(id+"F24.wireOp",EDGE,"E108.right")])]});
            var Q13;
            Q13=makeQuery(id+"F25.opExtrude","SWEPT_EDGE",EDGE,{"disambiguationData":[OSD([sQuery(id+"F24.wireOp",EDGE,"E108.top"),sQuery(id+"F24.wireOp",EDGE,"E108.right")])]});
            var Q14;
            Q14=makeQuery(id+"F25.opExtrude","SWEPT_EDGE",EDGE,{"disambiguationData":[OSD([sQuery(id+"F24.wireOp",EDGE,"E109.top"),sQuery(id+"F24.wireOp",EDGE,"E109.right")])]});
            var Q15;
            Q15=makeQuery(id+"F25.opExtrude","SWEPT_EDGE",EDGE,{"disambiguationData":[OSD([sQuery(id+"F24.wireOp",EDGE,"E108.bottom"),sQuery(id+"F24.wireOp",EDGE,"E108.left")])]});
            fillet(context, id + "F26", {"entities" : qUnion([Q0, Q1, Q2, Q3, Q4, Q5, Q6, Q7, Q8, Q9, Q10, Q11, Q12, Q13, Q14, Q15]), "radius" : 1 * mm, "allowEdgeOverflow" : false});
        }
        {
            var Q0;
            Q0=makeQuery(id+"F25.opExtrude","CAP_EDGE",EDGE,{"disambiguationData":[OSD([sQuery(id+"F24.wireOp",EDGE,"E94.top")])],"isStart":false});
            var Q1;
            Q1=makeQuery(id+"F25.opExtrude","CAP_EDGE",EDGE,{"disambiguationData":[OSD([sQuery(id+"F24.wireOp",EDGE,"E94.bottom")])],"isStart":false});
            var Q2;
            Q2=makeQuery(id+"F25.opExtrude","CAP_EDGE",EDGE,{"disambiguationData":[OSD([sQuery(id+"F24.wireOp",EDGE,"E93.top")])],"isStart":false});
            var Q3;
            Q3=makeQuery(id+"F25.opExtrude","CAP_EDGE",EDGE,{"disambiguationData":[OSD([sQuery(id+"F24.wireOp",EDGE,"E93.bottom")])],"isStart":false});
            var Q4;
            Q4=makeQuery(id+"F25.opExtrude","CAP_EDGE",EDGE,{"disambiguationData":[OSD([sQuery(id+"F24.wireOp",EDGE,"E95.bottom")])],"isStart":false});
            var Q5;
            Q5=makeQuery(id+"F25.opExtrude","CAP_EDGE",EDGE,{"disambiguationData":[OSD([sQuery(id+"F24.wireOp",EDGE,"E95.top")])],"isStart":false});
            var Q6;
            Q6=makeQuery(id+"F25.opExtrude","CAP_EDGE",EDGE,{"disambiguationData":[OSD([sQuery(id+"F24.wireOp",EDGE,"E96.top")])],"isStart":false});
            var Q7;
            Q7=makeQuery(id+"F25.opExtrude","CAP_EDGE",EDGE,{"disambiguationData":[OSD([sQuery(id+"F24.wireOp",EDGE,"E96.bottom")])],"isStart":false});
            chamfer(context, id + "F27", {"entities" : qUnion([Q0, Q1, Q2, Q3, Q4, Q5, Q6, Q7]), "width" : 1 * mm, "tangentPropagation" : true});
        }
    });
